# Revit family: Internal block_71_280_DH_1R1A
name_source: partatom
category: Оборудование
units: mm (PartAtom-declared; Revit-internal decimal feet)

## family parameters
Всегда вертикально = Да
Классификация = Нет
На основе рабочей плоскости = Нет
Общий = Нет
При загрузке вырезать с полостями = Нет
Размер круглого соединителя = Использовать диаметр
Тип детали = Нормальный
Точка принадлежности помещению = Нет

## types (9) — shared parameters
00_20_Manufacturer = BLAUBERG
00_20_Name = Internal block
Casing Material = Steel, galvanized
Grid Material = Mesh, steel, painted,  white
Load Classification = HVAC
Maintenance zone material = <По категории>
Maximum Air Flow = 0.0 л/с
dd = 10 мм
Изготовитель = BLAUBERG
zero-valued in all types: Отметка по умолчанию

## per-type parameters (varying)
| type | A | B | Bb | C | D | Db | E | F | G | H | Height | I | Length | Power | Weight | Width | dg | dr |
| BLHV-71-I-DH-AC/1R1A | 1445 мм | 680 мм | 610 мм | 260 мм | 1337 мм | 1417 мм | 515 мм | 1156 мм | 197 мм | 1156 мм | 260 мм | 207 мм | 1445 мм | 340 Вт | 46.00 кг | 680 мм | 16 мм | 10 мм |
| BLHV-80-I-DH-AC/1R1A | 1445 мм | 680 мм | 610 мм | 260 мм | 1337 мм | 1417 мм | 515 мм | 1156 мм | 197 мм | 1156 мм | 260 мм | 207 мм | 1445 мм | 340 Вт | 46.00 кг | 680 мм | 16 мм | 10 мм |
| BLHV-90-I-DH-AC/1R1A | 1445 мм | 680 мм | 610 мм | 260 мм | 1337 мм | 1417 мм | 515 мм | 1156 мм | 197 мм | 1156 мм | 260 мм | 207 мм | 1445 мм | 340 Вт | 46.00 кг | 680 мм | 16 мм | 10 мм |
| BLHV-100-I-DH-AC/1R1A | 1190 мм | 620 мм | 550 мм | 370 мм | 1038 мм | 1118 мм | 588 мм | 740 мм | 267 мм | 920 мм | 370 мм | 290 мм | 1190 мм | 450 Вт | 47.00 кг | 620 мм | 16 мм | 10 мм |
| BLHV-120-I-DH-AC/1R1A | 1190 мм | 620 мм | 550 мм | 370 мм | 1038 мм | 1118 мм | 588 мм | 740 мм | 267 мм | 920 мм | 370 мм | 290 мм | 1190 мм | 450 Вт | 47.00 кг | 620 мм | 16 мм | 10 мм |
| BLHV-150-I-DH-AC/1R1A | 1190 мм | 620 мм | 550 мм | 370 мм | 1038 мм | 1118 мм | 588 мм | 740 мм | 267 мм | 920 мм | 370 мм | 290 мм | 1190 мм | 450 Вт | 47.00 кг | 620 мм | 16 мм | 10 мм |
| BLHV-200-I-DH-AC/1R1A | 1440 мм | 811 мм | 741 мм | 448 мм | 1162 мм | 1242 мм | 771 мм | 930 мм | 180 мм | 1186 мм | 448 мм | 320 мм | 1440 мм | 1200 Вт | 102.00 кг | 811 мм | 22 мм | 13 мм |
| BLHV-250-I-DH-AC/1R1A | 1440 мм | 811 мм | 741 мм | 448 мм | 1162 мм | 1242 мм | 771 мм | 930 мм | 180 мм | 1186 мм | 448 мм | 320 мм | 1440 мм | 1200 Вт | 102.00 кг | 811 мм | 22 мм | 13 мм |
| BLHV-280-I-DH-AC/1R1A | 1440 мм | 811 мм | 741 мм | 448 мм | 1162 мм | 1242 мм | 771 мм | 930 мм | 180 мм | 1186 мм | 448 мм | 320 мм | 1440 мм | 1200 Вт | 102.00 кг | 811 мм | 22 мм | 13 мм |

note: column(s) folded — value = type name in every type: 00_20_Type
